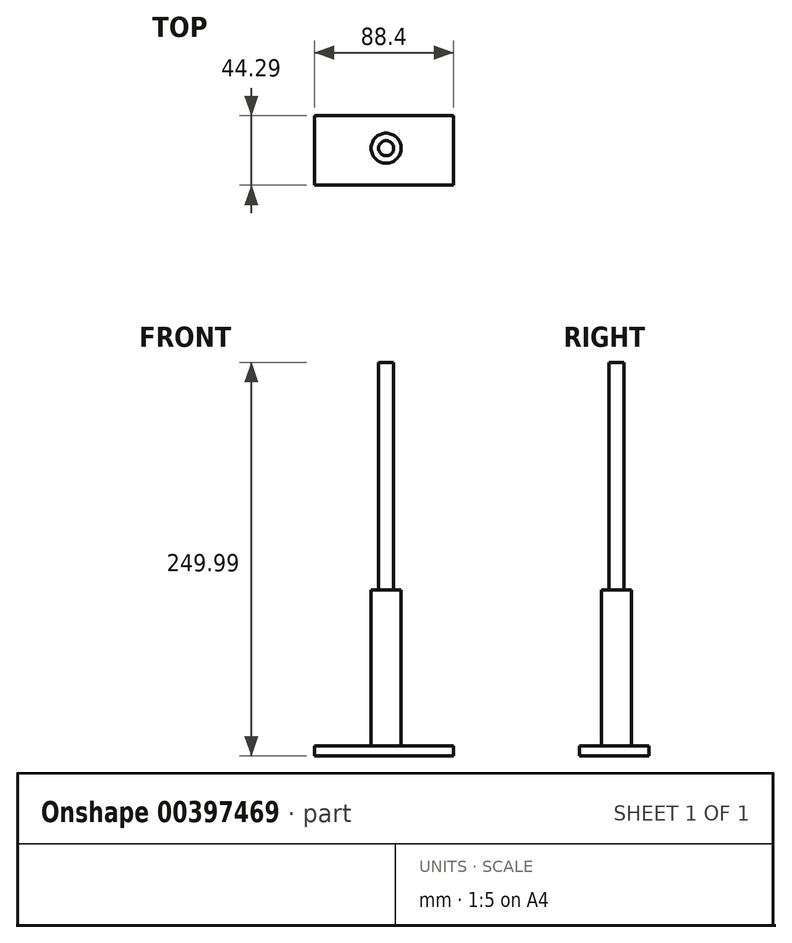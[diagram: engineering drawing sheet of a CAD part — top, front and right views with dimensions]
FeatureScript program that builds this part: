
annotation { "Feature Type Name" : "Feature", "Feature Type Description" : "" }
export const myFeature = defineFeature(function(context is Context, id is Id, definition is map)
    precondition{}
    {
        {
            var Q0;
            Q0=qCreatedBy(makeId("Top.planeOp"),FACE);
            var sketch = newSketch(context, id + "F0", { "sketchPlane" : qUnion([Q0])});
            skLineSegment(sketch, "E0.bottom", {"start": v(42.76, 0) * mm, "end": v(-45.64, 0) * mm});
            skLineSegment(sketch, "E0.top", {"start": v(42.76, -44.3) * mm, "end": v(-45.64, -44.3) * mm});
            skLineSegment(sketch, "E0.left", {"start": v(42.76, 0) * mm, "end": v(42.76, -44.3) * mm});
            skLineSegment(sketch, "E0.right", {"start": v(-45.64, 0) * mm, "end": v(-45.64, -44.3) * mm});
            skSolve(sketch);
        }
        {
            var Q0;
            Q0 = qSketchRegion(id + "F0", true);
            extrude(context, id + "F1", {"entities" : qUnion([Q0]), "depth" : 6.35 * mm});
        }
        {
            var Q0;
            Q0=makeQuery(id+"F1.opExtrude","CAP_FACE",FACE,{"disambiguationData":[OSD([sQuery(id+"F0.wireOp",EDGE,"E0.bottom"),sQuery(id+"F0.wireOp",EDGE,"E0.top"),sQuery(id+"F0.wireOp",EDGE,"E0.left"),sQuery(id+"F0.wireOp",EDGE,"E0.right")])],"isStart":false});
            var sketch = newSketch(context, id + "F2", { "sketchPlane" : qUnion([Q0])});
            skCircle(sketch, "E1", {"center": v(0, -20.74) * mm, "radius": 9.55 * mm});
            skSolve(sketch);
        }
        {
            var Q0;
            Q0 = qSketchRegion(id + "F2", true);
            extrude(context, id + "F3", {"entities" : qUnion([Q0]), "operationType" : NewBodyOperationType.ADD, "endBound" : BoundingType.THROUGH_ALL, "depth" : 25.4 * mm});
        }
        {
            var Q0;
            Q0=makeQuery(id+"F3.opExtrude","CAP_FACE",FACE,{"disambiguationData":[OSD([sQuery(id+"F2.wireOp",EDGE,"E1")])],"isStart":false});
            var sketch = newSketch(context, id + "F4", { "sketchPlane" : qUnion([Q0])});
            skCircle(sketch, "E2", {"center": v(0, -20.74) * mm, "radius": 4.8 * mm});
            skSolve(sketch);
        }
        {
            var Q0;
            Q0 = qSketchRegion(id + "F4", true);
            extrude(context, id + "F5", {"entities" : qUnion([Q0]), "operationType" : NewBodyOperationType.ADD, "endBound" : BoundingType.THROUGH_ALL, "depth" : 25.4 * mm});
        }
    });
